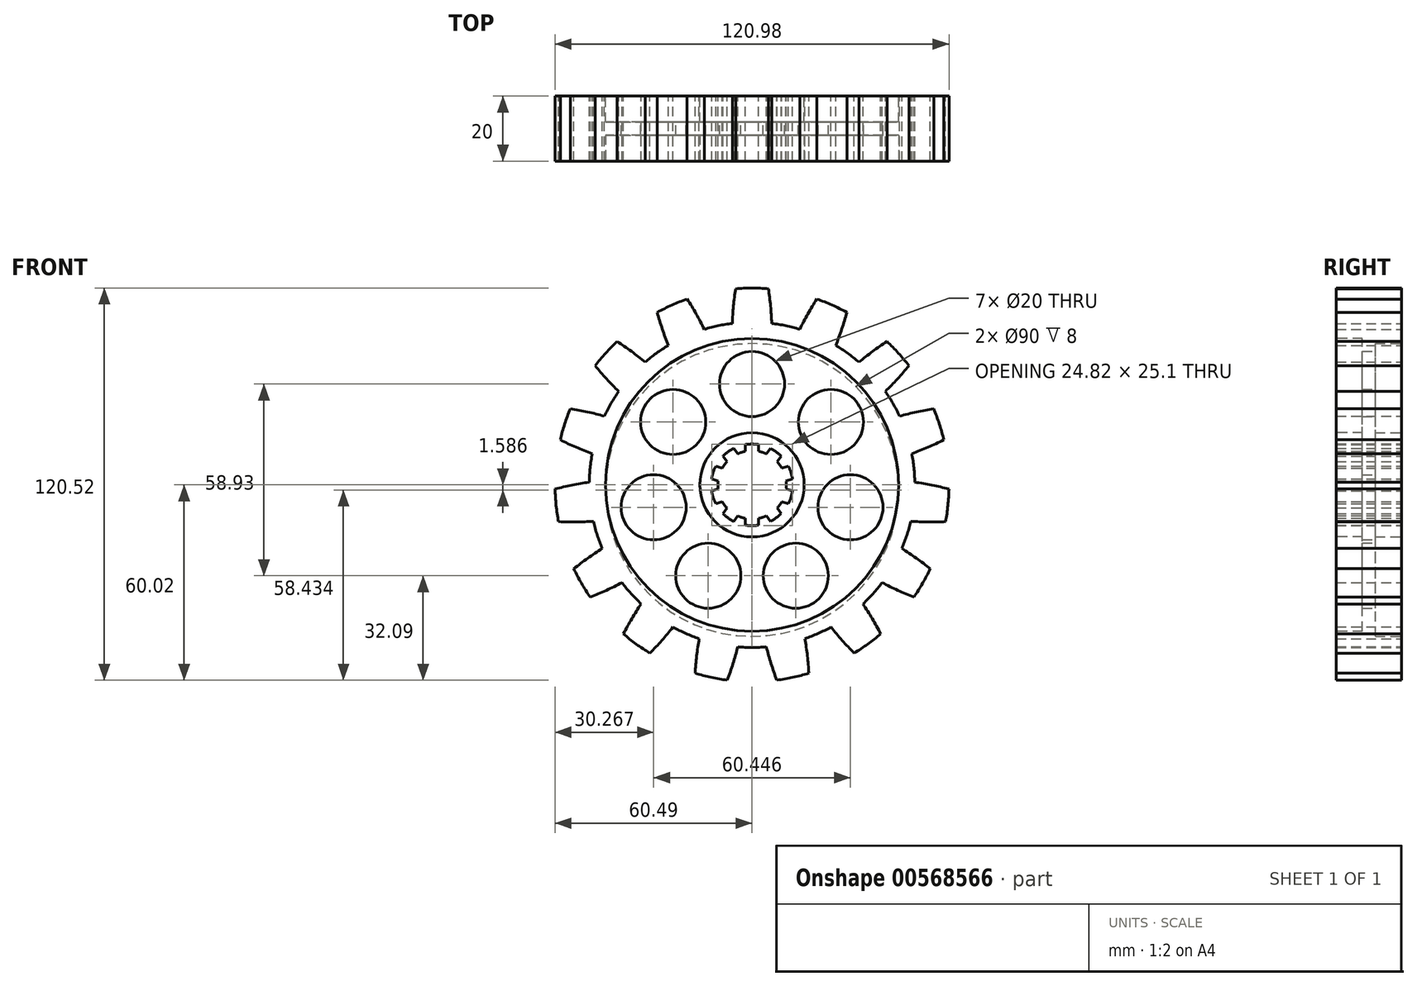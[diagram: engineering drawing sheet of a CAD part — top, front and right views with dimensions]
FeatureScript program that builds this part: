
annotation { "Feature Type Name" : "Feature", "Feature Type Description" : "" }
export const myFeature = defineFeature(function(context is Context, id is Id, definition is map)
    precondition{}
    {
        {
            var Q0;
            Q0=qCreatedBy(makeId("Front.planeOp"),FACE);
            var sketch = newSketch(context, id + "F0", { "sketchPlane" : qUnion([Q0])});
            skCircle(sketch, "E0", {"center": v(0, 0) * mm, "radius": 50 * mm});
            skLineSegment(sketch, "E1", {"start": v(-16.39, 46.5) * mm, "end": v(83.9, 46.5) * mm, "construction": true});
            skLineSegment(sketch, "E2", {"start": v(83.9, 46.5) * mm, "end": v(83.9, 27.65) * mm, "construction": true});
            skLineSegment(sketch, "E3", {"start": v(83.9, 46.5) * mm, "end": v(83.9, 51.66) * mm, "construction": true});
            skLineSegment(sketch, "E4", {"start": v(0, -2.7) * mm, "end": v(0, 89.14) * mm, "construction": true});
            skLineSegment(sketch, "E5", {"start": v(0, 50) * mm, "end": v(-34.34, 50) * mm, "construction": true});
            skArc(sketch, "E6", {"start": v(-5.04, 60.29) * mm, "mid": v(-5.7, 54.98) * mm, "end": v(-6.05, 49.63) * mm});
            skArc(sketch, "E7.MirrorCS", {"start": v(5.04, 60.29) * mm, "mid": v(5.7, 54.98) * mm, "end": v(6.05, 49.63) * mm});
            skArc(sketch, "E8.trimOffspring", {"start": v(5.04, 60.29) * mm, "mid": v(0, 60.5) * mm, "end": v(-5.04, 60.29) * mm});
            skArc(sketch, "E9.1.0", {"start": v(-19.92, 57.13) * mm, "mid": v(-24.6, 55.27) * mm, "end": v(-29.12, 53.03) * mm});
            skArc(sketch, "E9.2.0", {"start": v(-41.43, 44.09) * mm, "mid": v(-44.96, 40.48) * mm, "end": v(-48.17, 36.6) * mm});
            skArc(sketch, "E10.3.3.0", {"start": v(-55.78, 23.42) * mm, "mid": v(-57.54, 18.7) * mm, "end": v(-58.9, 13.84) * mm});
            skArc(sketch, "E10.3.4.0", {"start": v(-60.49, -1.3) * mm, "mid": v(-60.17, -6.32) * mm, "end": v(-59.43, -11.31) * mm});
            skArc(sketch, "E10.3.5.0", {"start": v(-54.73, -25.78) * mm, "mid": v(-52.4, -30.25) * mm, "end": v(-49.7, -34.5) * mm});
            skArc(sketch, "E10.3.6.0", {"start": v(-39.51, -45.81) * mm, "mid": v(-35.56, -48.95) * mm, "end": v(-31.36, -51.74) * mm});
            skArc(sketch, "E10.3.7.0", {"start": v(-17.46, -57.93) * mm, "mid": v(-12.58, -59.18) * mm, "end": v(-7.6, -60.02) * mm});
            skArc(sketch, "E10.3.8.0", {"start": v(7.6, -60.02) * mm, "mid": v(12.58, -59.18) * mm, "end": v(17.46, -57.93) * mm});
            skArc(sketch, "E10.3.9.0", {"start": v(31.36, -51.74) * mm, "mid": v(35.56, -48.95) * mm, "end": v(39.51, -45.81) * mm});
            skArc(sketch, "E10.3.10.0", {"start": v(49.7, -34.5) * mm, "mid": v(52.4, -30.25) * mm, "end": v(54.73, -25.78) * mm});
            skArc(sketch, "E10.3.11.0", {"start": v(59.43, -11.31) * mm, "mid": v(60.17, -6.32) * mm, "end": v(60.49, -1.3) * mm});
            skArc(sketch, "E10.3.12.0", {"start": v(58.9, 13.84) * mm, "mid": v(57.54, 18.7) * mm, "end": v(55.78, 23.42) * mm});
            skArc(sketch, "E10.3.13.0", {"start": v(48.17, 36.6) * mm, "mid": v(44.96, 40.48) * mm, "end": v(41.43, 44.09) * mm});
            skArc(sketch, "E10.3.14.0", {"start": v(29.12, 53.03) * mm, "mid": v(24.6, 55.27) * mm, "end": v(19.92, 57.13) * mm});
            skArc(sketch, "E11.1.0", {"start": v(-29.12, 53.03) * mm, "mid": v(-27.57, 47.9) * mm, "end": v(-25.71, 42.88) * mm});
            skArc(sketch, "E11.1.2", {"start": v(-19.92, 57.13) * mm, "mid": v(-17.15, 52.54) * mm, "end": v(-14.66, 47.8) * mm});
            skArc(sketch, "E11.2.0", {"start": v(-48.17, 36.6) * mm, "mid": v(-44.67, 32.55) * mm, "end": v(-40.93, 28.72) * mm});
            skArc(sketch, "E11.2.2", {"start": v(-41.43, 44.09) * mm, "mid": v(-37.04, 41.02) * mm, "end": v(-32.84, 37.7) * mm});
            skArc(sketch, "E11.3.0", {"start": v(-58.9, 13.84) * mm, "mid": v(-54.05, 11.57) * mm, "end": v(-49.07, 9.59) * mm});
            skArc(sketch, "E11.3.2", {"start": v(-55.78, 23.42) * mm, "mid": v(-50.52, 22.4) * mm, "end": v(-45.34, 21.09) * mm});
            skArc(sketch, "E11.4.0", {"start": v(-59.43, -11.31) * mm, "mid": v(-54.08, -11.42) * mm, "end": v(-48.73, -11.2) * mm});
            skArc(sketch, "E11.4.2", {"start": v(-60.49, -1.3) * mm, "mid": v(-55.27, -0.08) * mm, "end": v(-50, 0.82) * mm});
            skArc(sketch, "E11.5.0", {"start": v(-49.7, -34.5) * mm, "mid": v(-44.76, -32.42) * mm, "end": v(-39.96, -30.05) * mm});
            skArc(sketch, "E11.5.2", {"start": v(-54.73, -25.78) * mm, "mid": v(-50.46, -22.55) * mm, "end": v(-46, -19.58) * mm});
            skArc(sketch, "E11.6.0", {"start": v(-31.36, -51.74) * mm, "mid": v(-27.7, -47.83) * mm, "end": v(-24.28, -43.7) * mm});
            skArc(sketch, "E11.6.2", {"start": v(-39.51, -45.81) * mm, "mid": v(-36.93, -41.13) * mm, "end": v(-34.06, -36.6) * mm});
            skArc(sketch, "E11.7.0", {"start": v(-7.6, -60.02) * mm, "mid": v(-5.85, -54.96) * mm, "end": v(-4.4, -49.8) * mm});
            skArc(sketch, "E11.7.2", {"start": v(-17.46, -57.93) * mm, "mid": v(-17, -52.6) * mm, "end": v(-16.23, -47.3) * mm});
            skArc(sketch, "E11.8.0", {"start": v(17.46, -57.93) * mm, "mid": v(17, -52.6) * mm, "end": v(16.23, -47.3) * mm});
            skArc(sketch, "E11.8.2", {"start": v(7.6, -60.02) * mm, "mid": v(5.85, -54.96) * mm, "end": v(4.4, -49.8) * mm});
            skArc(sketch, "E11.9.0", {"start": v(39.51, -45.81) * mm, "mid": v(36.93, -41.13) * mm, "end": v(34.06, -36.6) * mm});
            skArc(sketch, "E11.9.2", {"start": v(31.36, -51.74) * mm, "mid": v(27.7, -47.83) * mm, "end": v(24.28, -43.7) * mm});
            skArc(sketch, "E11.10.0", {"start": v(54.73, -25.78) * mm, "mid": v(50.46, -22.55) * mm, "end": v(46, -19.58) * mm});
            skArc(sketch, "E11.10.2", {"start": v(49.7, -34.5) * mm, "mid": v(44.76, -32.42) * mm, "end": v(39.96, -30.05) * mm});
            skArc(sketch, "E11.11.0", {"start": v(60.49, -1.3) * mm, "mid": v(55.27, -0.08) * mm, "end": v(50, 0.82) * mm});
            skArc(sketch, "E11.11.2", {"start": v(59.43, -11.31) * mm, "mid": v(54.08, -11.42) * mm, "end": v(48.73, -11.2) * mm});
            skArc(sketch, "E11.12.0", {"start": v(55.78, 23.42) * mm, "mid": v(50.52, 22.4) * mm, "end": v(45.34, 21.09) * mm});
            skArc(sketch, "E11.12.2", {"start": v(58.9, 13.84) * mm, "mid": v(54.05, 11.57) * mm, "end": v(49.07, 9.59) * mm});
            skArc(sketch, "E11.13.0", {"start": v(41.43, 44.09) * mm, "mid": v(37.04, 41.02) * mm, "end": v(32.84, 37.7) * mm});
            skArc(sketch, "E11.13.2", {"start": v(48.17, 36.6) * mm, "mid": v(44.67, 32.55) * mm, "end": v(40.93, 28.72) * mm});
            skArc(sketch, "E11.14.0", {"start": v(19.92, 57.13) * mm, "mid": v(17.15, 52.54) * mm, "end": v(14.66, 47.8) * mm});
            skArc(sketch, "E11.14.2", {"start": v(29.12, 53.03) * mm, "mid": v(27.57, 47.9) * mm, "end": v(25.71, 42.88) * mm});
            skSolve(sketch);
        }
        {
            var Q0;
            {var subQ0=sQuery(id+"F0.wireOp",EDGE,"E0");var subQ18=makeQuery(id+"F0.imprint","INTERSECT",VERTEX,{"derivedFrom":[subQ0,sQuery(id+"F0.wireOp",EDGE,"E11.11.0")]});Q0=makeQuery(id+"F0.imprint","IMPRINT",FACE,{"disambiguationData":[TD([[makeQuery(id+"F0.imprint","IMPRINT",EDGE,{"disambiguationData":[TD([[subQ18,-1.0]])],"derivedFrom":subQ0}),1.0]])]});}
            var Q1;
            {var subQ0=sQuery(id+"F0.wireOp",EDGE,"E11.1.0");Q1=makeQuery(id+"F0.imprint","IMPRINT",FACE,{"disambiguationData":[TD([[makeQuery(id+"F0.imprint","IMPRINT",EDGE,{"derivedFrom":subQ0}),1.0]])]});}
            var Q2;
            {var subQ0=sQuery(id+"F0.wireOp",EDGE,"E6");Q2=makeQuery(id+"F0.imprint","IMPRINT",FACE,{"disambiguationData":[TD([[makeQuery(id+"F0.imprint","IMPRINT",EDGE,{"derivedFrom":subQ0}),1.0]])]});}
            var Q3;
            {var subQ0=sQuery(id+"F0.wireOp",EDGE,"E11.14.0");Q3=makeQuery(id+"F0.imprint","IMPRINT",FACE,{"disambiguationData":[TD([[makeQuery(id+"F0.imprint","IMPRINT",EDGE,{"derivedFrom":subQ0}),1.0]])]});}
            var Q4;
            {var subQ0=sQuery(id+"F0.wireOp",EDGE,"E11.13.0");Q4=makeQuery(id+"F0.imprint","IMPRINT",FACE,{"disambiguationData":[TD([[makeQuery(id+"F0.imprint","IMPRINT",EDGE,{"derivedFrom":subQ0}),1.0]])]});}
            var Q5;
            {var subQ0=sQuery(id+"F0.wireOp",EDGE,"E11.12.0");Q5=makeQuery(id+"F0.imprint","IMPRINT",FACE,{"disambiguationData":[TD([[makeQuery(id+"F0.imprint","IMPRINT",EDGE,{"derivedFrom":subQ0}),1.0]])]});}
            var Q6;
            {var subQ0=sQuery(id+"F0.wireOp",EDGE,"E11.11.0");Q6=makeQuery(id+"F0.imprint","IMPRINT",FACE,{"disambiguationData":[TD([[makeQuery(id+"F0.imprint","IMPRINT",EDGE,{"derivedFrom":subQ0}),1.0]])]});}
            var Q7;
            {var subQ0=sQuery(id+"F0.wireOp",EDGE,"E11.10.0");Q7=makeQuery(id+"F0.imprint","IMPRINT",FACE,{"disambiguationData":[TD([[makeQuery(id+"F0.imprint","IMPRINT",EDGE,{"derivedFrom":subQ0}),1.0]])]});}
            var Q8;
            {var subQ0=sQuery(id+"F0.wireOp",EDGE,"E11.9.0");Q8=makeQuery(id+"F0.imprint","IMPRINT",FACE,{"disambiguationData":[TD([[makeQuery(id+"F0.imprint","IMPRINT",EDGE,{"derivedFrom":subQ0}),1.0]])]});}
            var Q9;
            {var subQ0=sQuery(id+"F0.wireOp",EDGE,"E11.8.0");Q9=makeQuery(id+"F0.imprint","IMPRINT",FACE,{"disambiguationData":[TD([[makeQuery(id+"F0.imprint","IMPRINT",EDGE,{"derivedFrom":subQ0}),1.0]])]});}
            var Q10;
            {var subQ0=sQuery(id+"F0.wireOp",EDGE,"E11.7.0");Q10=makeQuery(id+"F0.imprint","IMPRINT",FACE,{"disambiguationData":[TD([[makeQuery(id+"F0.imprint","IMPRINT",EDGE,{"derivedFrom":subQ0}),1.0]])]});}
            var Q11;
            {var subQ0=sQuery(id+"F0.wireOp",EDGE,"E11.6.0");Q11=makeQuery(id+"F0.imprint","IMPRINT",FACE,{"disambiguationData":[TD([[makeQuery(id+"F0.imprint","IMPRINT",EDGE,{"derivedFrom":subQ0}),1.0]])]});}
            var Q12;
            {var subQ0=sQuery(id+"F0.wireOp",EDGE,"E11.5.0");Q12=makeQuery(id+"F0.imprint","IMPRINT",FACE,{"disambiguationData":[TD([[makeQuery(id+"F0.imprint","IMPRINT",EDGE,{"derivedFrom":subQ0}),1.0]])]});}
            var Q13;
            {var subQ0=sQuery(id+"F0.wireOp",EDGE,"E11.4.0");Q13=makeQuery(id+"F0.imprint","IMPRINT",FACE,{"disambiguationData":[TD([[makeQuery(id+"F0.imprint","IMPRINT",EDGE,{"derivedFrom":subQ0}),1.0]])]});}
            var Q14;
            {var subQ0=sQuery(id+"F0.wireOp",EDGE,"E11.3.0");Q14=makeQuery(id+"F0.imprint","IMPRINT",FACE,{"disambiguationData":[TD([[makeQuery(id+"F0.imprint","IMPRINT",EDGE,{"derivedFrom":subQ0}),1.0]])]});}
            var Q15;
            {var subQ0=sQuery(id+"F0.wireOp",EDGE,"E11.2.0");Q15=makeQuery(id+"F0.imprint","IMPRINT",FACE,{"disambiguationData":[TD([[makeQuery(id+"F0.imprint","IMPRINT",EDGE,{"derivedFrom":subQ0}),1.0]])]});}
            extrude(context, id + "F1", {"entities" : qUnion([Q0, Q1, Q2, Q3, Q4, Q5, Q6, Q7, Q8, Q9, Q10, Q11, Q12, Q13, Q14, Q15]), "depth" : 20 * mm, "offsetDistance" : 25 * mm});
        }
        {
            var Q0;
            Q0=qCreatedBy(makeId("Front.planeOp"),FACE);
            var sketch = newSketch(context, id + "F2", { "sketchPlane" : qUnion([Q0])});
            skCircle(sketch, "E12", {"center": v(0, 0) * mm, "radius": 10.5 * mm});
            skArc(sketch, "E13", {"start": v(2.05, 12.38) * mm, "mid": v(0, 12.55) * mm, "end": v(-2.05, 12.38) * mm});
            skLineSegment(sketch, "E14", {"start": v(-2.05, 10.3) * mm, "end": v(-2.05, 12.38) * mm});
            skLineSegment(sketch, "E15", {"start": v(2.05, 10.3) * mm, "end": v(2.05, 12.38) * mm});
            skPoint(sketch, "E16.end.orphan", {"position": v(2.05, 0) * mm});
            skLineSegment(sketch, "E17.1.0", {"start": v(-7.71, 7.13) * mm, "end": v(-8.94, 8.81) * mm});
            skArc(sketch, "E17.1.1", {"start": v(-5.62, 11.22) * mm, "mid": v(-7.38, 10.15) * mm, "end": v(-8.94, 8.81) * mm});
            skLineSegment(sketch, "E17.1.2", {"start": v(-4.4, 9.54) * mm, "end": v(-5.62, 11.22) * mm});
            skLineSegment(sketch, "E17.2.0", {"start": v(-10.43, 1.23) * mm, "end": v(-12.4, 1.88) * mm});
            skArc(sketch, "E17.2.1", {"start": v(-11.14, 5.78) * mm, "mid": v(-11.94, 3.88) * mm, "end": v(-12.4, 1.88) * mm});
            skLineSegment(sketch, "E17.2.2", {"start": v(-9.16, 5.13) * mm, "end": v(-11.14, 5.78) * mm});
            skLineSegment(sketch, "E17.3.0", {"start": v(-9.16, -5.13) * mm, "end": v(-11.14, -5.78) * mm});
            skArc(sketch, "E17.3.1", {"start": v(-12.4, -1.88) * mm, "mid": v(-11.94, -3.88) * mm, "end": v(-11.14, -5.78) * mm});
            skLineSegment(sketch, "E17.3.2", {"start": v(-10.43, -1.23) * mm, "end": v(-12.4, -1.88) * mm});
            skLineSegment(sketch, "E17.4.0", {"start": v(-4.4, -9.54) * mm, "end": v(-5.62, -11.22) * mm});
            skArc(sketch, "E17.4.1", {"start": v(-8.94, -8.81) * mm, "mid": v(-7.38, -10.15) * mm, "end": v(-5.62, -11.22) * mm});
            skLineSegment(sketch, "E17.4.2", {"start": v(-7.71, -7.13) * mm, "end": v(-8.94, -8.81) * mm});
            skLineSegment(sketch, "E17.5.0", {"start": v(2.05, -10.3) * mm, "end": v(2.05, -12.38) * mm});
            skArc(sketch, "E17.5.1", {"start": v(-2.05, -12.38) * mm, "mid": v(0, -12.55) * mm, "end": v(2.05, -12.38) * mm});
            skLineSegment(sketch, "E17.5.2", {"start": v(-2.05, -10.3) * mm, "end": v(-2.05, -12.38) * mm});
            skLineSegment(sketch, "E17.6.0", {"start": v(7.71, -7.13) * mm, "end": v(8.94, -8.81) * mm});
            skArc(sketch, "E17.6.1", {"start": v(5.62, -11.22) * mm, "mid": v(7.38, -10.15) * mm, "end": v(8.94, -8.81) * mm});
            skLineSegment(sketch, "E17.6.2", {"start": v(4.4, -9.54) * mm, "end": v(5.62, -11.22) * mm});
            skLineSegment(sketch, "E17.7.0", {"start": v(10.43, -1.23) * mm, "end": v(12.4, -1.88) * mm});
            skArc(sketch, "E17.7.1", {"start": v(11.14, -5.78) * mm, "mid": v(11.94, -3.88) * mm, "end": v(12.4, -1.88) * mm});
            skLineSegment(sketch, "E17.7.2", {"start": v(9.16, -5.13) * mm, "end": v(11.14, -5.78) * mm});
            skLineSegment(sketch, "E17.8.0", {"start": v(9.16, 5.13) * mm, "end": v(11.14, 5.78) * mm});
            skArc(sketch, "E17.8.1", {"start": v(12.4, 1.88) * mm, "mid": v(11.94, 3.88) * mm, "end": v(11.14, 5.78) * mm});
            skLineSegment(sketch, "E17.8.2", {"start": v(10.43, 1.23) * mm, "end": v(12.4, 1.88) * mm});
            skLineSegment(sketch, "E17.9.0", {"start": v(4.4, 9.54) * mm, "end": v(5.62, 11.22) * mm});
            skArc(sketch, "E17.9.1", {"start": v(8.94, 8.81) * mm, "mid": v(7.38, 10.15) * mm, "end": v(5.62, 11.22) * mm});
            skLineSegment(sketch, "E17.9.2", {"start": v(7.71, 7.13) * mm, "end": v(8.94, 8.81) * mm});
            skSolve(sketch);
        }
        {
            var Q0;
            {var subQ0=sQuery(id+"F2.wireOp",EDGE,"E12");var subQ8=makeQuery(id+"F2.imprint","INTERSECT",VERTEX,{"derivedFrom":[subQ0,sQuery(id+"F2.wireOp",EDGE,"E17.8.0")]});Q0=makeQuery(id+"F2.imprint","IMPRINT",FACE,{"disambiguationData":[TD([[makeQuery(id+"F2.imprint","IMPRINT",EDGE,{"disambiguationData":[TD([[subQ8,1.0]])],"derivedFrom":subQ0}),1.0]])]});}
            var Q1;
            {var subQ0=sQuery(id+"F2.wireOp",EDGE,"E17.1.0");Q1=makeQuery(id+"F2.imprint","IMPRINT",FACE,{"disambiguationData":[TD([[makeQuery(id+"F2.imprint","IMPRINT",EDGE,{"derivedFrom":subQ0}),-1.0]])]});}
            var Q2;
            {var subQ0=sQuery(id+"F2.wireOp",EDGE,"E17.2.0");Q2=makeQuery(id+"F2.imprint","IMPRINT",FACE,{"disambiguationData":[TD([[makeQuery(id+"F2.imprint","IMPRINT",EDGE,{"derivedFrom":subQ0}),-1.0]])]});}
            var Q3;
            Q3=makeQuery(id+"F2.imprint","IMPRINT",FACE,{"disambiguationData":[TD([[makeQuery(id+"F2.imprint","IMPRINT",EDGE,{"derivedFrom":sQuery(id+"F2.wireOp",EDGE,"E13")}),1.0]])]});
            var Q4;
            {var subQ0=sQuery(id+"F2.wireOp",EDGE,"E17.9.0");Q4=makeQuery(id+"F2.imprint","IMPRINT",FACE,{"disambiguationData":[TD([[makeQuery(id+"F2.imprint","IMPRINT",EDGE,{"derivedFrom":subQ0}),-1.0]])]});}
            var Q5;
            {var subQ0=sQuery(id+"F2.wireOp",EDGE,"E17.8.0");Q5=makeQuery(id+"F2.imprint","IMPRINT",FACE,{"disambiguationData":[TD([[makeQuery(id+"F2.imprint","IMPRINT",EDGE,{"derivedFrom":subQ0}),-1.0]])]});}
            var Q6;
            {var subQ0=sQuery(id+"F2.wireOp",EDGE,"E17.7.0");Q6=makeQuery(id+"F2.imprint","IMPRINT",FACE,{"disambiguationData":[TD([[makeQuery(id+"F2.imprint","IMPRINT",EDGE,{"derivedFrom":subQ0}),-1.0]])]});}
            var Q7;
            {var subQ0=sQuery(id+"F2.wireOp",EDGE,"E17.6.0");Q7=makeQuery(id+"F2.imprint","IMPRINT",FACE,{"disambiguationData":[TD([[makeQuery(id+"F2.imprint","IMPRINT",EDGE,{"derivedFrom":subQ0}),-1.0]])]});}
            var Q8;
            {var subQ0=sQuery(id+"F2.wireOp",EDGE,"E17.5.0");Q8=makeQuery(id+"F2.imprint","IMPRINT",FACE,{"disambiguationData":[TD([[makeQuery(id+"F2.imprint","IMPRINT",EDGE,{"derivedFrom":subQ0}),-1.0]])]});}
            var Q9;
            {var subQ0=sQuery(id+"F2.wireOp",EDGE,"E17.4.0");Q9=makeQuery(id+"F2.imprint","IMPRINT",FACE,{"disambiguationData":[TD([[makeQuery(id+"F2.imprint","IMPRINT",EDGE,{"derivedFrom":subQ0}),-1.0]])]});}
            var Q10;
            {var subQ0=sQuery(id+"F2.wireOp",EDGE,"E17.3.0");Q10=makeQuery(id+"F2.imprint","IMPRINT",FACE,{"disambiguationData":[TD([[makeQuery(id+"F2.imprint","IMPRINT",EDGE,{"derivedFrom":subQ0}),-1.0]])]});}
            extrude(context, id + "F3", {"entities" : qUnion([Q0, Q1, Q2, Q3, Q4, Q5, Q6, Q7, Q8, Q9, Q10]), "operationType" : NewBodyOperationType.REMOVE, "depth" : 20 * mm, "offsetDistance" : 25 * mm});
        }
        {
            var Q0;
            Q0=qCreatedBy(makeId("Front.planeOp"),FACE);
            var sketch = newSketch(context, id + "F4", { "sketchPlane" : qUnion([Q0])});
            skCircle(sketch, "E18", {"center": v(0, 31) * mm, "radius": 10 * mm});
            skCircle(sketch, "E19.1.0", {"center": v(-24.24, 19.33) * mm, "radius": 10 * mm});
            skCircle(sketch, "E19.2.0", {"center": v(-30.22, -6.9) * mm, "radius": 10 * mm});
            skCircle(sketch, "E19.3.0", {"center": v(-13.45, -27.93) * mm, "radius": 10 * mm});
            skCircle(sketch, "E19.4.0", {"center": v(13.45, -27.93) * mm, "radius": 10 * mm});
            skCircle(sketch, "E19.5.0", {"center": v(30.22, -6.9) * mm, "radius": 10 * mm});
            skCircle(sketch, "E19.6.0", {"center": v(24.24, 19.33) * mm, "radius": 10 * mm});
            skPoint(sketch, "E19.center", {"position": v(0, 0) * mm});
            skSolve(sketch);
        }
        {
            var Q0;
            Q0=makeQuery(id+"F4.imprint","IMPRINT",FACE,{"disambiguationData":[TD([[makeQuery(id+"F4.imprint","IMPRINT",EDGE,{"derivedFrom":sQuery(id+"F4.wireOp",EDGE,"E19.6.0")}),1.0]])]});
            var Q1;
            Q1=makeQuery(id+"F4.imprint","IMPRINT",FACE,{"disambiguationData":[TD([[makeQuery(id+"F4.imprint","IMPRINT",EDGE,{"derivedFrom":sQuery(id+"F4.wireOp",EDGE,"E18")}),1.0]])]});
            var Q2;
            Q2=makeQuery(id+"F4.imprint","IMPRINT",FACE,{"disambiguationData":[TD([[makeQuery(id+"F4.imprint","IMPRINT",EDGE,{"derivedFrom":sQuery(id+"F4.wireOp",EDGE,"E19.1.0")}),1.0]])]});
            var Q3;
            Q3=makeQuery(id+"F4.imprint","IMPRINT",FACE,{"disambiguationData":[TD([[makeQuery(id+"F4.imprint","IMPRINT",EDGE,{"derivedFrom":sQuery(id+"F4.wireOp",EDGE,"E19.2.0")}),1.0]])]});
            var Q4;
            Q4=makeQuery(id+"F4.imprint","IMPRINT",FACE,{"disambiguationData":[TD([[makeQuery(id+"F4.imprint","IMPRINT",EDGE,{"derivedFrom":sQuery(id+"F4.wireOp",EDGE,"E19.3.0")}),1.0]])]});
            var Q5;
            Q5=makeQuery(id+"F4.imprint","IMPRINT",FACE,{"disambiguationData":[TD([[makeQuery(id+"F4.imprint","IMPRINT",EDGE,{"derivedFrom":sQuery(id+"F4.wireOp",EDGE,"E19.4.0")}),1.0]])]});
            var Q6;
            Q6=makeQuery(id+"F4.imprint","IMPRINT",FACE,{"disambiguationData":[TD([[makeQuery(id+"F4.imprint","IMPRINT",EDGE,{"derivedFrom":sQuery(id+"F4.wireOp",EDGE,"E19.5.0")}),1.0]])]});
            extrude(context, id + "F5", {"entities" : qUnion([Q0, Q1, Q2, Q3, Q4, Q5, Q6]), "operationType" : NewBodyOperationType.REMOVE, "depth" : 25 * mm, "offsetDistance" : 25 * mm});
        }
        {
            var Q0;
            Q0=qCreatedBy(makeId("Front.planeOp"),FACE);
            var sketch = newSketch(context, id + "F6", { "sketchPlane" : qUnion([Q0])});
            skCircle(sketch, "E20", {"center": v(0, 0) * mm, "radius": 16 * mm});
            skCircle(sketch, "E21", {"center": v(0, -1.59) * mm, "radius": 45 * mm});
            skSolve(sketch);
        }
        {
            var Q0;
            Q0=makeQuery(id+"F6.imprint","IMPRINT",FACE,{"disambiguationData":[TD([[makeQuery(id+"F6.imprint","IMPRINT",EDGE,{"derivedFrom":sQuery(id+"F6.wireOp",EDGE,"E20")}),-1.0]])]});
            extrude(context, id + "F7", {"entities" : qUnion([Q0]), "operationType" : NewBodyOperationType.REMOVE, "depth" : 8 * mm, "offsetDistance" : 25 * mm});
        }
        {
            var Q0;
            Q0=qCreatedBy(makeId("Right.planeOp"),FACE);
            var sketch = newSketch(context, id + "F8", { "sketchPlane" : qUnion([Q0])});
            skLineSegment(sketch, "E22.bottom", {"start": v(-36.25, 16) * mm, "end": v(-12, 16) * mm});
            skLineSegment(sketch, "E22.top", {"start": v(-36.25, 45) * mm, "end": v(-12, 45) * mm});
            skLineSegment(sketch, "E22.left", {"start": v(-36.25, 16) * mm, "end": v(-36.25, 45) * mm});
            skLineSegment(sketch, "E22.right", {"start": v(-12, 16) * mm, "end": v(-12, 45) * mm});
            skLineSegment(sketch, "E23.bottom", {"start": v(0, 0) * mm, "end": v(-76.6, 0) * mm, "construction": true});
            skLineSegment(sketch, "E23.top", {"start": v(0, 0) * mm, "end": v(-76.6, 0) * mm, "construction": true});
            skLineSegment(sketch, "E23.left", {"start": v(0, 0) * mm, "end": v(0, 0) * mm});
            skLineSegment(sketch, "E23.right", {"start": v(-76.6, 0) * mm, "end": v(-76.6, 0) * mm});
            skSolve(sketch);
        }
        {
            var Q0;
            Q0=makeQuery(id+"F8.imprint","IMPRINT",FACE,{"disambiguationData":[TD([[makeQuery(id+"F8.imprint","IMPRINT",EDGE,{"derivedFrom":sQuery(id+"F8.wireOp",EDGE,"E22.bottom")}),1.0]])]});
            var Q1;
            Q1=sQuery(id+"F8.wireOp",EDGE,"E23.top");
            revolve(context, id + "F9", {"operationType" : NewBodyOperationType.REMOVE, "entities" : qUnion([Q0]), "axis" : qUnion([Q1]), "revolveType" : RevolveType.FULL, "oppositeDirection" : true});
        }
    });
